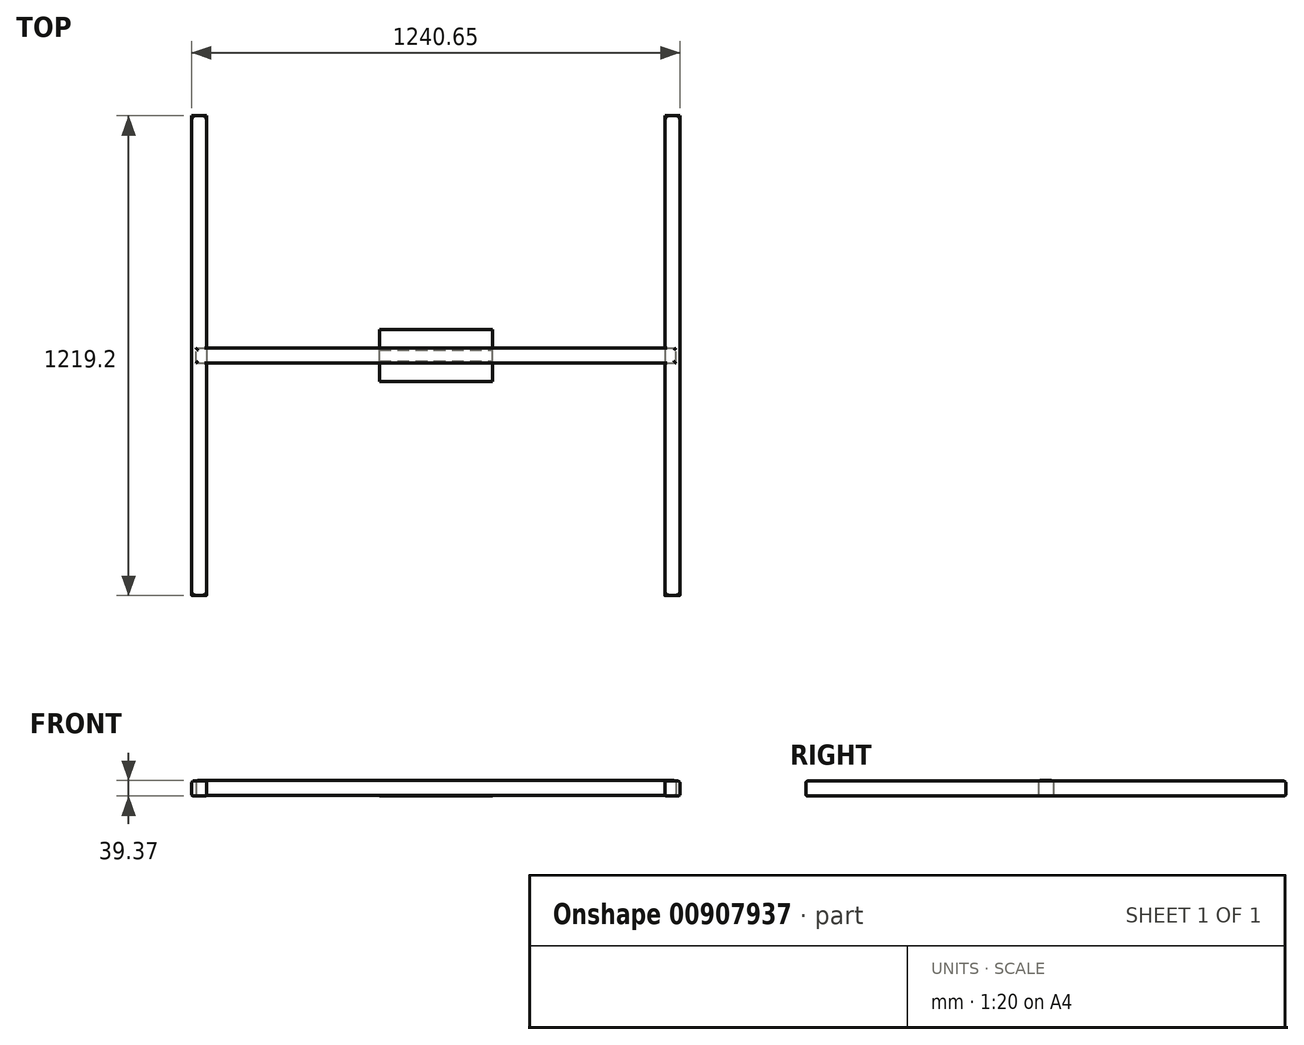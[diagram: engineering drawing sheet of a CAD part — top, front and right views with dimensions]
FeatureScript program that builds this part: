
annotation { "Feature Type Name" : "Feature", "Feature Type Description" : "" }
export const myFeature = defineFeature(function(context is Context, id is Id, definition is map)
    precondition{}
    {
        {
            var Q0;
            Q0=qCreatedBy(makeId("Top.planeOp"),FACE);
            var sketch = newSketch(context, id + "F0", { "sketchPlane" : qUnion([Q0])});
            skLineSegment(sketch, "E0.bottom", {"start": v(-609.6, -19.05) * mm, "end": v(609.6, -19.05) * mm});
            skLineSegment(sketch, "E0.top", {"start": v(-609.6, 19.05) * mm, "end": v(609.6, 19.05) * mm});
            skLineSegment(sketch, "E0.left", {"start": v(-609.6, -19.05) * mm, "end": v(-609.6, 19.05) * mm});
            skLineSegment(sketch, "E0.right", {"start": v(609.6, -19.05) * mm, "end": v(609.6, 19.05) * mm});
            skPoint(sketch, "E0.middle", {"position": v(0, 0) * mm});
            skSolve(sketch);
        }
        {
            var Q0;
            Q0=makeQuery(id+"F0.imprint","IMPRINT",FACE,{"disambiguationData":[TD([[makeQuery(id+"F0.imprint","IMPRINT",EDGE,{"derivedFrom":sQuery(id+"F0.wireOp",EDGE,"E0.bottom")}),1.0]])]});
            var Q1;
            Q1 = qSketchRegion(id + "F0", true);
            extrude(context, id + "F1", {"entities" : qUnion([Q0, Q1]), "depth" : 38.1 * mm, "offsetDistance" : 25.4 * mm});
        }
        {
            var Q0;
            Q0=makeQuery(id+"F1.opExtrude","CAP_FACE",FACE,{"disambiguationData":[OSD([sQuery(id+"F0.wireOp",EDGE,"E0.bottom"),sQuery(id+"F0.wireOp",EDGE,"E0.top"),sQuery(id+"F0.wireOp",EDGE,"E0.left"),sQuery(id+"F0.wireOp",EDGE,"E0.right")])],"isStart":false});
            var Q1;
            Q1=makeQuery(id+"F1.opExtrude","CAP_EDGE",EDGE,{"disambiguationData":[OSD([sQuery(id+"F0.wireOp",EDGE,"E0.top")])],"isStart":false});
            fillet(context, id + "F2", {"entities" : qUnion([Q0, Q1]), "radius" : 5.08 * mm, "tangentPropagation" : true, "allowEdgeOverflow" : false});
        }
        {
            var Q0;
            Q0=makeQuery(id+"F1.opExtrude","CAP_EDGE",EDGE,{"disambiguationData":[OSD([sQuery(id+"F0.wireOp",EDGE,"E0.left")])],"isStart":true});
            var Q1;
            Q1=makeQuery(id+"F1.opExtrude","CAP_EDGE",EDGE,{"disambiguationData":[OSD([sQuery(id+"F0.wireOp",EDGE,"E0.top")])],"isStart":true});
            var Q2;
            Q2=makeQuery(id+"F1.opExtrude","CAP_EDGE",EDGE,{"disambiguationData":[OSD([sQuery(id+"F0.wireOp",EDGE,"E0.bottom")])],"isStart":true});
            var Q3;
            Q3=makeQuery(id+"F1.opExtrude","CAP_EDGE",EDGE,{"disambiguationData":[OSD([sQuery(id+"F0.wireOp",EDGE,"E0.right")])],"isStart":true});
            fillet(context, id + "F3", {"entities" : qUnion([Q0, Q1, Q2, Q3]), "radius" : 5.08 * mm, "tangentPropagation" : true, "allowEdgeOverflow" : false});
        }
        {
            var Q0;
            Q0=qCreatedBy(makeId("Top.planeOp"),FACE);
            var sketch = newSketch(context, id + "F4", { "sketchPlane" : qUnion([Q0])});
            skLineSegment(sketch, "E1.bottom", {"start": v(-143.5, -66.13) * mm, "end": v(143.5, -66.13) * mm});
            skLineSegment(sketch, "E1.top", {"start": v(-143.5, 66.13) * mm, "end": v(143.5, 66.13) * mm});
            skLineSegment(sketch, "E1.left", {"start": v(-143.5, -66.13) * mm, "end": v(-143.5, 66.13) * mm});
            skLineSegment(sketch, "E1.right", {"start": v(143.5, -66.13) * mm, "end": v(143.5, 66.13) * mm});
            skPoint(sketch, "E1.middle", {"position": v(0, 0) * mm});
            skSolve(sketch);
        }
        {
            var Q0;
            Q0=makeQuery(id+"F4.imprint","IMPRINT",FACE,{"disambiguationData":[TD([[makeQuery(id+"F4.imprint","IMPRINT",EDGE,{"derivedFrom":sQuery(id+"F4.wireOp",EDGE,"E1.bottom")}),1.0]])]});
            extrude(context, id + "F5", {"entities" : qUnion([Q0]), "operationType" : NewBodyOperationType.ADD, "oppositeDirection" : true, "depth" : 1.27 * mm, "offsetDistance" : 25.4 * mm});
        }
        {
            var Q0;
            Q0=makeQuery(id+"F5.opExtrude","CAP_FACE",FACE,{"disambiguationData":[OSD([sQuery(id+"F4.wireOp",EDGE,"E1.bottom"),sQuery(id+"F4.wireOp",EDGE,"E1.top"),sQuery(id+"F4.wireOp",EDGE,"E1.left"),sQuery(id+"F4.wireOp",EDGE,"E1.right")])],"isStart":false});
            var sketch = newSketch(context, id + "F6", { "sketchPlane" : qUnion([Q0])});
            skLineSegment(sketch, "E2.bottom", {"start": v(-582.41, -609.6) * mm, "end": v(-620.51, -609.6) * mm});
            skLineSegment(sketch, "E2.top", {"start": v(-582.41, 609.6) * mm, "end": v(-620.51, 609.6) * mm});
            skLineSegment(sketch, "E2.left", {"start": v(-582.41, -609.6) * mm, "end": v(-582.41, 609.6) * mm});
            skLineSegment(sketch, "E2.right", {"start": v(-620.51, -609.6) * mm, "end": v(-620.51, 609.6) * mm});
            skPoint(sketch, "E2.middle", {"position": v(-601.46, 0) * mm});
            skPoint(sketch, "E2.middle.positionSnap0", {"position": v(-143.5, 0) * mm});
            skPoint(sketch, "E2.centerSnap0", {"position": v(-143.5, 0) * mm});
            skLineSegment(sketch, "E3.bottom", {"start": v(582.04, -609.6) * mm, "end": v(620.14, -609.6) * mm});
            skLineSegment(sketch, "E3.top", {"start": v(582.04, 609.6) * mm, "end": v(620.14, 609.6) * mm});
            skLineSegment(sketch, "E3.left", {"start": v(582.04, -609.6) * mm, "end": v(582.04, 609.6) * mm});
            skLineSegment(sketch, "E3.right", {"start": v(620.14, -609.6) * mm, "end": v(620.14, 609.6) * mm});
            skPoint(sketch, "E3.middle", {"position": v(601.09, 0) * mm});
            skSolve(sketch);
        }
        {
            var Q0;
            Q0=makeQuery(id+"F6.imprint","IMPRINT",FACE,{"disambiguationData":[TD([[makeQuery(id+"F6.imprint","IMPRINT",EDGE,{"derivedFrom":sQuery(id+"F6.wireOp",EDGE,"E2.bottom")}),-1.0]])]});
            var Q1;
            Q1 = qSketchRegion(id + "F6", true);
            extrude(context, id + "F7", {"entities" : qUnion([Q0, Q1]), "oppositeDirection" : true, "depth" : 38.1 * mm, "offsetDistance" : 25.4 * mm});
        }
        {
            var Q0;
            Q0=makeQuery(id+"F7.opExtrude","CAP_EDGE",EDGE,{"disambiguationData":[OSD([sQuery(id+"F6.wireOp",EDGE,"E2.right")])],"isStart":true});
            var Q1;
            Q1=makeQuery(id+"F7.opExtrude","CAP_EDGE",EDGE,{"disambiguationData":[OSD([sQuery(id+"F6.wireOp",EDGE,"E2.left")])],"isStart":true});
            var Q2;
            Q2=makeQuery(id+"F7.opExtrude","CAP_EDGE",EDGE,{"disambiguationData":[OSD([sQuery(id+"F6.wireOp",EDGE,"E2.top")])],"isStart":true});
            var Q3;
            Q3=makeQuery(id+"F7.opExtrude","CAP_EDGE",EDGE,{"disambiguationData":[OSD([sQuery(id+"F6.wireOp",EDGE,"E2.bottom")])],"isStart":true});
            var Q4;
            Q4=makeQuery(id+"F7.opExtrude","CAP_EDGE",EDGE,{"disambiguationData":[OSD([sQuery(id+"F6.wireOp",EDGE,"E3.bottom")])],"isStart":true});
            var Q5;
            Q5=makeQuery(id+"F7.opExtrude","CAP_EDGE",EDGE,{"disambiguationData":[OSD([sQuery(id+"F6.wireOp",EDGE,"E3.left")])],"isStart":true});
            var Q6;
            Q6=makeQuery(id+"F7.opExtrude","CAP_EDGE",EDGE,{"disambiguationData":[OSD([sQuery(id+"F6.wireOp",EDGE,"E3.right")])],"isStart":true});
            var Q7;
            Q7=makeQuery(id+"F7.opExtrude","CAP_EDGE",EDGE,{"disambiguationData":[OSD([sQuery(id+"F6.wireOp",EDGE,"E3.top")])],"isStart":true});
            var Q8;
            Q8=makeQuery(id+"F7.opExtrude","CAP_EDGE",EDGE,{"disambiguationData":[OSD([sQuery(id+"F6.wireOp",EDGE,"E2.top")])],"isStart":false});
            var Q9;
            Q9=makeQuery(id+"F7.opExtrude","CAP_EDGE",EDGE,{"disambiguationData":[OSD([sQuery(id+"F6.wireOp",EDGE,"E2.left")])],"isStart":false});
            var Q10;
            Q10=makeQuery(id+"F7.opExtrude","CAP_EDGE",EDGE,{"disambiguationData":[OSD([sQuery(id+"F6.wireOp",EDGE,"E2.right")])],"isStart":false});
            var Q11;
            Q11=makeQuery(id+"F7.opExtrude","CAP_EDGE",EDGE,{"disambiguationData":[OSD([sQuery(id+"F6.wireOp",EDGE,"E2.bottom")])],"isStart":false});
            var Q12;
            Q12=makeQuery(id+"F7.opExtrude","CAP_EDGE",EDGE,{"disambiguationData":[OSD([sQuery(id+"F6.wireOp",EDGE,"E3.bottom")])],"isStart":false});
            var Q13;
            Q13=makeQuery(id+"F7.opExtrude","CAP_EDGE",EDGE,{"disambiguationData":[OSD([sQuery(id+"F6.wireOp",EDGE,"E3.right")])],"isStart":false});
            var Q14;
            Q14=makeQuery(id+"F7.opExtrude","CAP_EDGE",EDGE,{"disambiguationData":[OSD([sQuery(id+"F6.wireOp",EDGE,"E3.left")])],"isStart":false});
            var Q15;
            Q15=makeQuery(id+"F7.opExtrude","CAP_EDGE",EDGE,{"disambiguationData":[OSD([sQuery(id+"F6.wireOp",EDGE,"E3.top")])],"isStart":false});
            fillet(context, id + "F8", {"entities" : qUnion([Q0, Q1, Q2, Q3, Q4, Q5, Q6, Q7, Q8, Q9, Q10, Q11, Q12, Q13, Q14, Q15]), "radius" : 5.08 * mm, "tangentPropagation" : true, "allowEdgeOverflow" : false});
        }
    });
